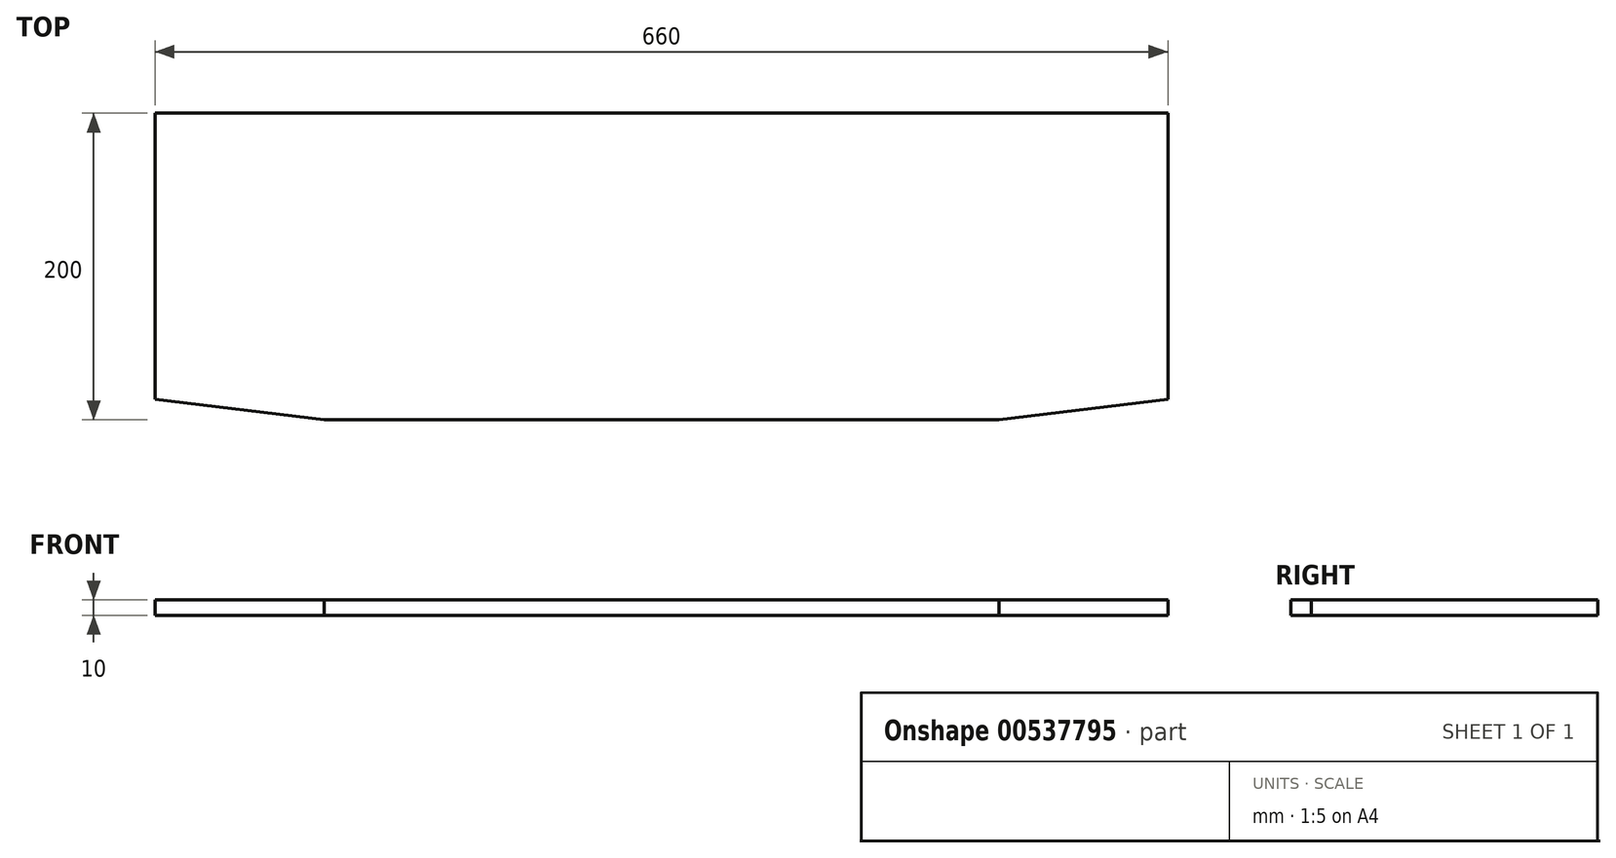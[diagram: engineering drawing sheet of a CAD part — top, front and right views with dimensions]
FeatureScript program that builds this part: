
annotation { "Feature Type Name" : "Feature", "Feature Type Description" : "" }
export const myFeature = defineFeature(function(context is Context, id is Id, definition is map)
    precondition{}
    {
        {
            var Q0;
            Q0=qCreatedBy(makeId("Top.planeOp"),FACE);
            var sketch = newSketch(context, id + "F0", { "sketchPlane" : qUnion([Q0])});
            skLineSegment(sketch, "E0.bottom", {"start": v(-330, 0) * mm, "end": v(330, 0) * mm});
            skLineSegment(sketch, "E0.top", {"start": v(-220, -200) * mm, "end": v(220, -200) * mm});
            skLineSegment(sketch, "E0.left", {"start": v(-330, 0) * mm, "end": v(-330, -186.5) * mm});
            skLineSegment(sketch, "E0.right", {"start": v(330, 0) * mm, "end": v(330, -186.5) * mm});
            skLineSegment(sketch, "E1", {"start": v(220, -200) * mm, "end": v(330, -186.5) * mm});
            skLineSegment(sketch, "E2", {"start": v(-330, -186.5) * mm, "end": v(-220, -200) * mm});
            skPoint(sketch, "E3", {"position": v(0, 0) * mm});
            skPoint(sketch, "E4", {"position": v(0, -200) * mm});
            skSolve(sketch);
        }
        {
            var Q0;
            Q0 = qSketchRegion(id + "F0", true);
            extrude(context, id + "F1", {"entities" : qUnion([Q0]), "depth" : 10 * mm, "offsetDistance" : 25 * mm});
        }
    });
